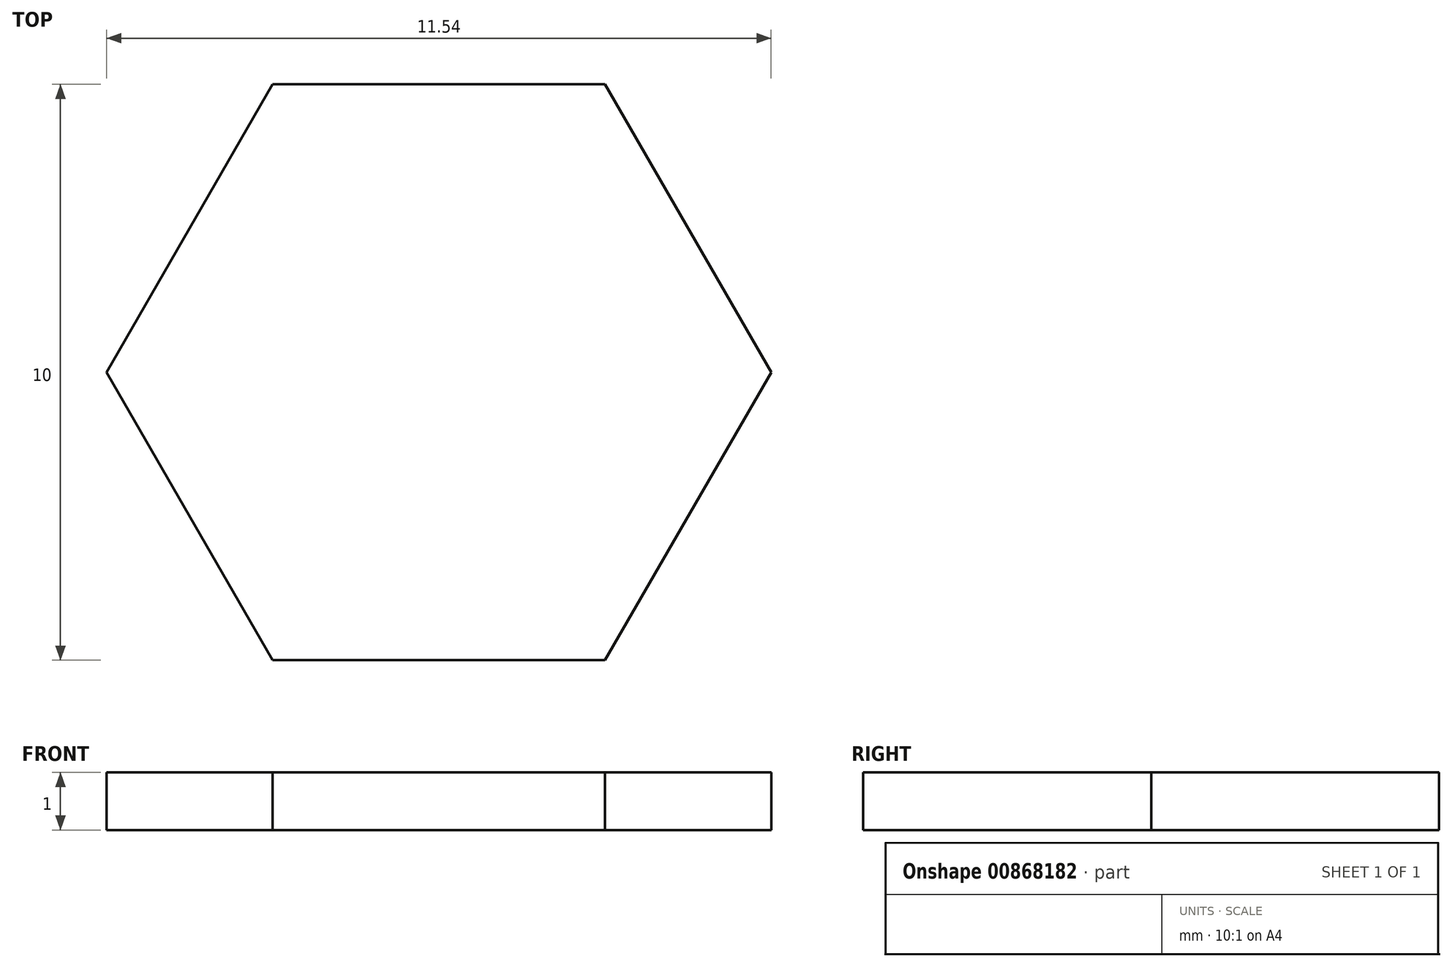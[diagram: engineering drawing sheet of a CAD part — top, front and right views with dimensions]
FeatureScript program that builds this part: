
annotation { "Feature Type Name" : "Feature", "Feature Type Description" : "" }
export const myFeature = defineFeature(function(context is Context, id is Id, definition is map)
    precondition{}
    {
        {
            var Q0;
            Q0=qCreatedBy(makeId("Top.planeOp"),FACE);
            var sketch = newSketch(context, id + "F0", { "sketchPlane" : qUnion([Q0])});
            skCircle(sketch, "E0.cCircle", {"center": v(0, 0) * mm, "radius": 5 * mm, "construction": true});
            skLineSegment(sketch, "E0.0", {"start": v(2.89, 5) * mm, "end": v(5.77, 0) * mm});
            skLineSegment(sketch, "E0.1", {"start": v(5.77, 0) * mm, "end": v(2.89, -5) * mm});
            skLineSegment(sketch, "E0.2", {"start": v(2.89, -5) * mm, "end": v(-2.89, -5) * mm});
            skLineSegment(sketch, "E0.3", {"start": v(-2.89, -5) * mm, "end": v(-5.77, 0) * mm});
            skLineSegment(sketch, "E0.4", {"start": v(-5.77, 0) * mm, "end": v(-2.89, 5) * mm});
            skLineSegment(sketch, "E0.5", {"start": v(-2.89, 5) * mm, "end": v(2.89, 5) * mm});
            skPoint(sketch, "E0.0.midPoint", {"position": v(4.33, 2.5) * mm});
            skSolve(sketch);
        }
        {
            var Q0;
            Q0 = qSketchRegion(id + "F0", true);
            extrude(context, id + "F1", {"entities" : qUnion([Q0]), "depth" : 1 * mm, "offsetDistance" : 25 * mm});
        }
    });
